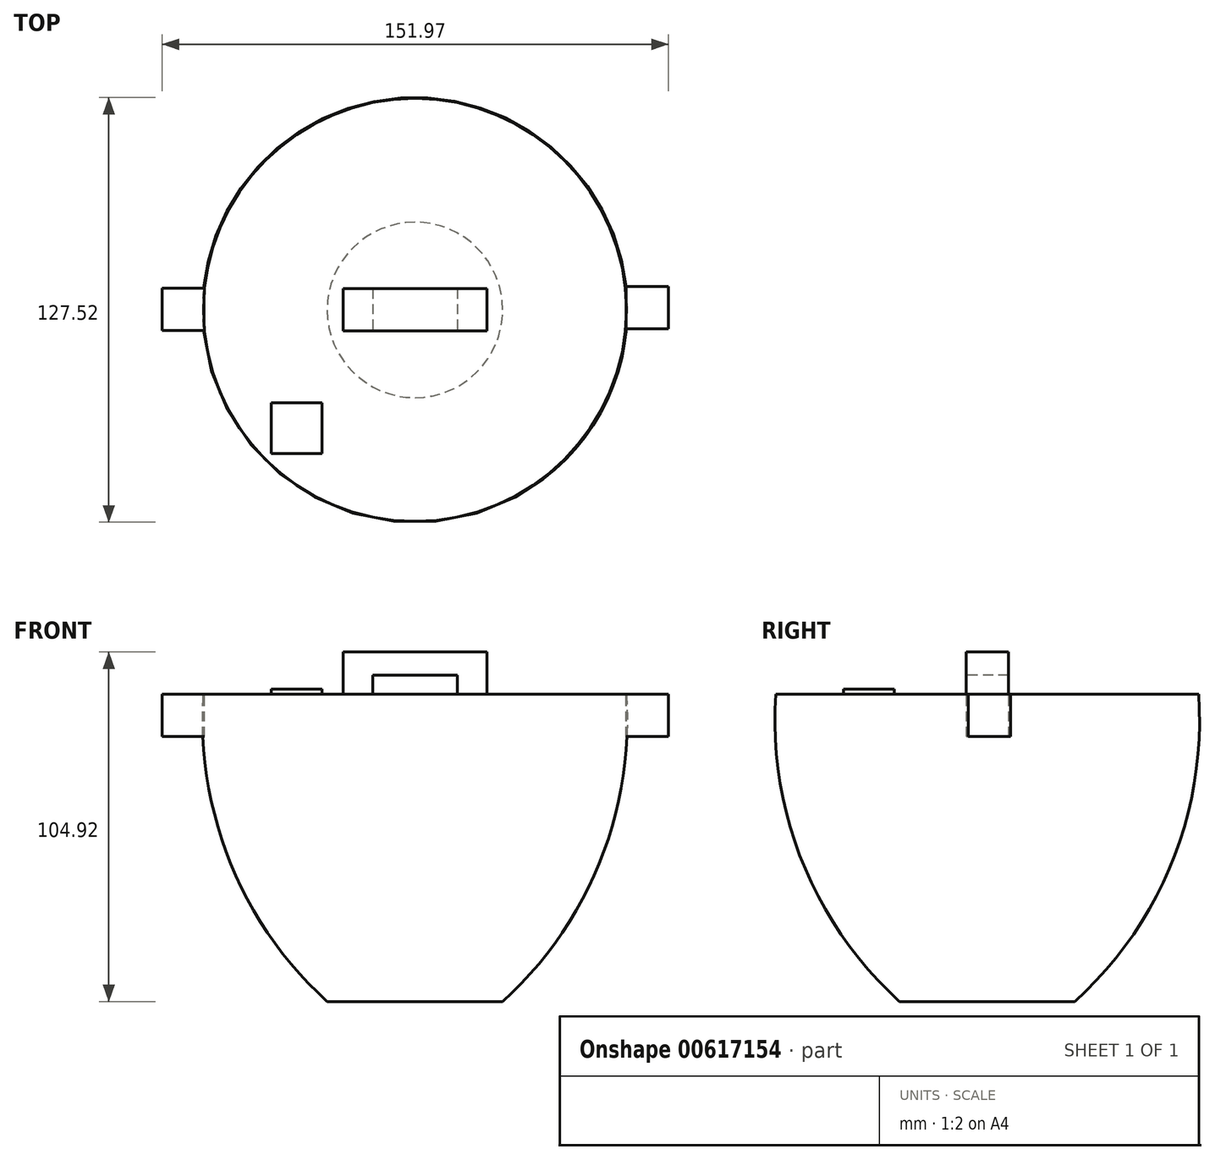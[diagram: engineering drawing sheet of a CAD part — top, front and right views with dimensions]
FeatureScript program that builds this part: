
annotation { "Feature Type Name" : "Feature", "Feature Type Description" : "" }
export const myFeature = defineFeature(function(context is Context, id is Id, definition is map)
    precondition{}
    {
        {
            var Q0;
            Q0=qCreatedBy(makeId("Right.planeOp"),FACE);
            var sketch = newSketch(context, id + "F0", { "sketchPlane" : qUnion([Q0])});
            skLineSegment(sketch, "E0", {"start": v(0, 40.9) * mm, "end": v(0, -51.32) * mm});
            skLineSegment(sketch, "E1", {"start": v(0, -51.32) * mm, "end": v(-26.35, -51.32) * mm});
            skArc(sketch, "E2", {"start": v(-63.5, 40.9) * mm, "mid": v(-55.5, -9.47) * mm, "end": v(-26.35, -51.32) * mm});
            skLineSegment(sketch, "E3", {"start": v(0, 40.9) * mm, "end": v(-63.5, 40.9) * mm});
            skSolve(sketch);
        }
        {
            var Q0;
            Q0 = qSketchRegion(id + "F0", true);
            var Q1;
            Q1=sQuery(id+"F0.wireOp",EDGE,"E0");
            revolve(context, id + "F1", {"entities" : qUnion([Q0]), "axis" : qUnion([Q1]), "revolveType" : RevolveType.FULL});
        }
        {
            var Q0;
            Q0=makeQuery(id+"F1.opRevolve","SWEPT_FACE",FACE,{"disambiguationData":[OSD([sQuery(id+"F0.wireOp",EDGE,"E3")])]});
            var sketch = newSketch(context, id + "F2", { "sketchPlane" : qUnion([Q0])});
            skLineSegment(sketch, "E4.bottom", {"start": v(-21.59, 6.35) * mm, "end": v(21.59, 6.35) * mm});
            skLineSegment(sketch, "E4.top", {"start": v(-21.59, -6.35) * mm, "end": v(21.59, -6.35) * mm});
            skLineSegment(sketch, "E4.left", {"start": v(-21.59, 6.35) * mm, "end": v(-21.59, -6.35) * mm});
            skLineSegment(sketch, "E4.right", {"start": v(21.59, 6.35) * mm, "end": v(21.59, -6.35) * mm});
            skPoint(sketch, "E4.middle", {"position": v(0, 0) * mm});
            skSolve(sketch);
        }
        {
            var Q0;
            Q0 = qSketchRegion(id + "F2", true);
            extrude(context, id + "F3", {"entities" : qUnion([Q0]), "depth" : 12.7 * mm, "offsetDistance" : 25.4 * mm});
        }
        {
            var Q0;
            Q0=makeQuery(id+"F3.opExtrude","SWEPT_FACE",FACE,{"disambiguationData":[OSD([sQuery(id+"F2.wireOp",EDGE,"E4.top")])]});
            var sketch = newSketch(context, id + "F4", { "sketchPlane" : qUnion([Q0])});
            skLineSegment(sketch, "E5", {"start": v(0, 40.9) * mm, "end": v(12.7, 40.9) * mm});
            skLineSegment(sketch, "E6", {"start": v(12.7, 40.9) * mm, "end": v(12.7, 46.66) * mm});
            skLineSegment(sketch, "E7", {"start": v(12.7, 46.66) * mm, "end": v(-12.7, 46.66) * mm});
            skLineSegment(sketch, "E8", {"start": v(-12.7, 46.66) * mm, "end": v(-12.7, 40.9) * mm});
            skLineSegment(sketch, "E9", {"start": v(-12.7, 40.9) * mm, "end": v(0, 40.9) * mm});
            skSolve(sketch);
        }
        {
            var Q0;
            Q0 = qSketchRegion(id + "F4", true);
            extrude(context, id + "F5", {"entities" : qUnion([Q0]), "operationType" : NewBodyOperationType.REMOVE, "oppositeDirection" : true, "depth" : 25.4 * mm, "offsetDistance" : 25.4 * mm});
        }
        {
            var Q0;
            Q0=makeQuery(id+"F1.opRevolve","SWEPT_FACE",FACE,{"disambiguationData":[OSD([sQuery(id+"F0.wireOp",EDGE,"E3")])]});
            var sketch = newSketch(context, id + "F6", { "sketchPlane" : qUnion([Q0])});
            skLineSegment(sketch, "E10.bottom", {"start": v(-27.94, -27.94) * mm, "end": v(-43.18, -27.94) * mm});
            skLineSegment(sketch, "E10.top", {"start": v(-27.94, -43.18) * mm, "end": v(-43.18, -43.18) * mm});
            skLineSegment(sketch, "E10.left", {"start": v(-27.94, -27.94) * mm, "end": v(-27.94, -43.18) * mm});
            skLineSegment(sketch, "E10.right", {"start": v(-43.18, -27.94) * mm, "end": v(-43.18, -43.18) * mm});
            skPoint(sketch, "E10.middle", {"position": v(-35.56, -35.56) * mm});
            skSolve(sketch);
        }
        {
            var Q0;
            Q0 = qSketchRegion(id + "F6", true);
            extrude(context, id + "F7", {"entities" : qUnion([Q0]), "depth" : 1.52 * mm, "offsetDistance" : 25.4 * mm});
        }
        {
            var Q0;
            Q0=makeQuery(id+"F1.opRevolve","SWEPT_FACE",FACE,{"disambiguationData":[OSD([sQuery(id+"F0.wireOp",EDGE,"E3")])]});
            var sketch = newSketch(context, id + "F8", { "sketchPlane" : qUnion([Q0])});
            skLineSegment(sketch, "E11", {"start": v(-75.9, 0.12) * mm, "end": v(-75.9, 6.47) * mm});
            skLineSegment(sketch, "E12", {"start": v(-75.9, 6.47) * mm, "end": v(-63.17, 6.47) * mm});
            skLineSegment(sketch, "E13", {"start": v(-75.9, 0.12) * mm, "end": v(-75.9, -6.23) * mm});
            skLineSegment(sketch, "E14", {"start": v(-75.9, -6.23) * mm, "end": v(-63.2, -6.23) * mm});
            skArc(sketch, "E15", {"start": v(-63.17, 6.47) * mm, "mid": v(-63.38, 0.12) * mm, "end": v(-63.2, -6.23) * mm});
            skSolve(sketch);
        }
        {
            var Q0;
            {var subQ0=makeQuery(id+"F1.opRevolve","SWEPT_EDGE",EDGE,{"disambiguationData":[OSD([sQuery(id+"F0.wireOp",EDGE,"E2"),sQuery(id+"F0.wireOp",EDGE,"E3")])]});var subQ1=makeQuery(id+"F8.imprint","INTERSECT",VERTEX,{"derivedFrom":[subQ0,sQuery(id+"F8.wireOp",EDGE,"E12")]});Q0=makeQuery(id+"F8.imprint","IMPRINT",FACE,{"disambiguationData":[TD([[makeQuery(id+"F8.imprint","IMPRINT",EDGE,{"disambiguationData":[TD([[subQ1,1.0]])],"derivedFrom":subQ0}),1.0]])]});}
            var sketch = newSketch(context, id + "F9", { "sketchPlane" : qUnion([Q0])});
            skLineSegment(sketch, "E16", {"start": v(76.08, 0.69) * mm, "end": v(76.08, -5.66) * mm});
            skLineSegment(sketch, "E17", {"start": v(76.08, -5.66) * mm, "end": v(63.36, -5.66) * mm});
            skLineSegment(sketch, "E18", {"start": v(76.08, 0.69) * mm, "end": v(76.08, 7.04) * mm});
            skLineSegment(sketch, "E19", {"start": v(76.08, 7.04) * mm, "end": v(63.38, 7.04) * mm});
            skArc(sketch, "E20", {"start": v(63.36, -5.66) * mm, "mid": v(63.48, 0.68) * mm, "end": v(63.38, 7.04) * mm});
            skSolve(sketch);
        }
        {
            var Q0;
            Q0 = qSketchRegion(id + "F8", true);
            extrude(context, id + "F10", {"entities" : qUnion([Q0]), "oppositeDirection" : true, "depth" : 12.7 * mm, "offsetDistance" : 25.4 * mm});
        }
        {
            var Q0;
            Q0 = qSketchRegion(id + "F9", true);
            extrude(context, id + "F11", {"entities" : qUnion([Q0]), "oppositeDirection" : true, "depth" : 12.7 * mm, "offsetDistance" : 25.4 * mm});
        }
    });
